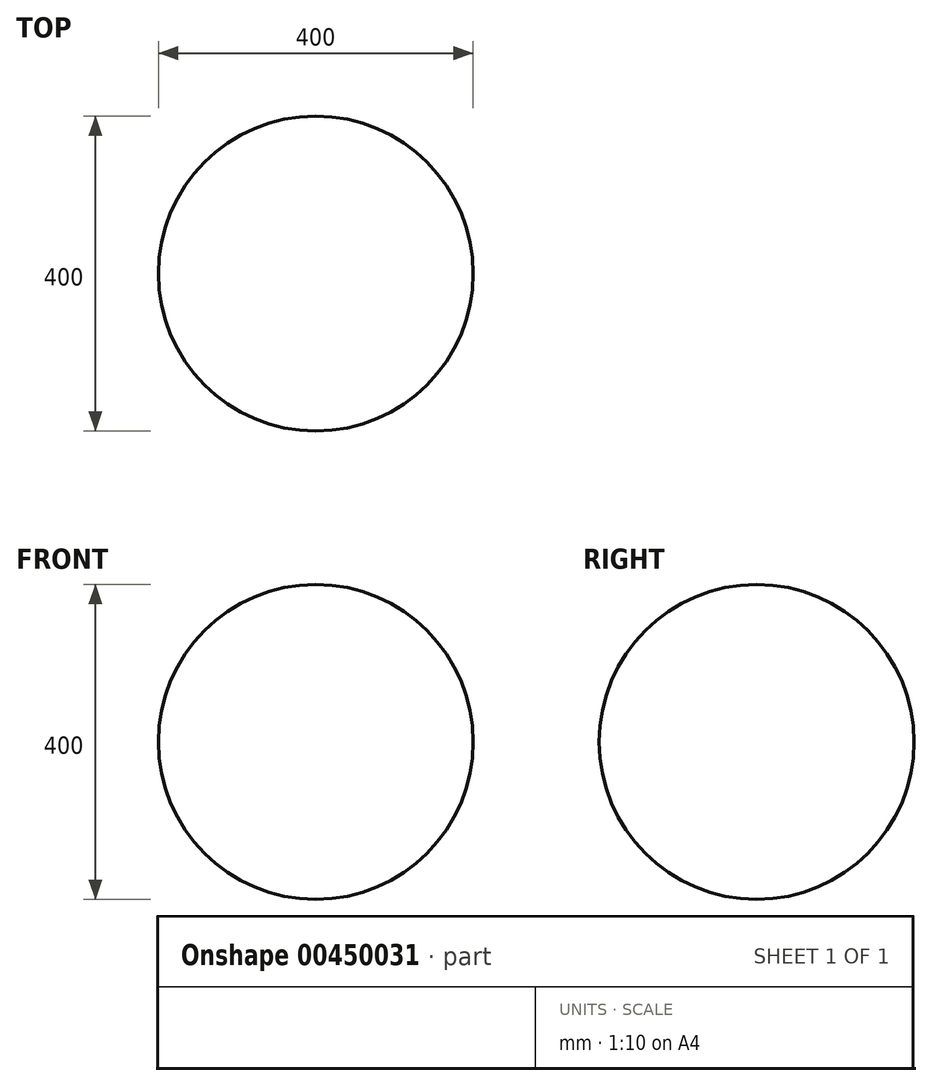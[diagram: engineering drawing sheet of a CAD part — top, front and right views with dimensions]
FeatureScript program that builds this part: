
annotation { "Feature Type Name" : "Feature", "Feature Type Description" : "" }
export const myFeature = defineFeature(function(context is Context, id is Id, definition is map)
    precondition{}
    {
        {
            var Q0;
            Q0=qCreatedBy(makeId("Top.planeOp"),FACE);
            var sketch = newSketch(context, id + "F0", { "sketchPlane" : qUnion([Q0])});
            skArc(sketch, "E0", {"start": v(0, -200) * mm, "mid": v(200, 0) * mm, "end": v(0, 200) * mm});
            skLineSegment(sketch, "E1", {"start": v(0, 200) * mm, "end": v(0, -200) * mm});
            skSolve(sketch);
        }
        {
            var Q0;
            Q0 = qSketchRegion(id + "F0", true);
            var Q1;
            Q1=sQuery(id+"F0.wireOp",EDGE,"E1");
            revolve(context, id + "F1", {"entities" : qUnion([Q0]), "axis" : qUnion([Q1]), "revolveType" : RevolveType.FULL});
        }
    });
